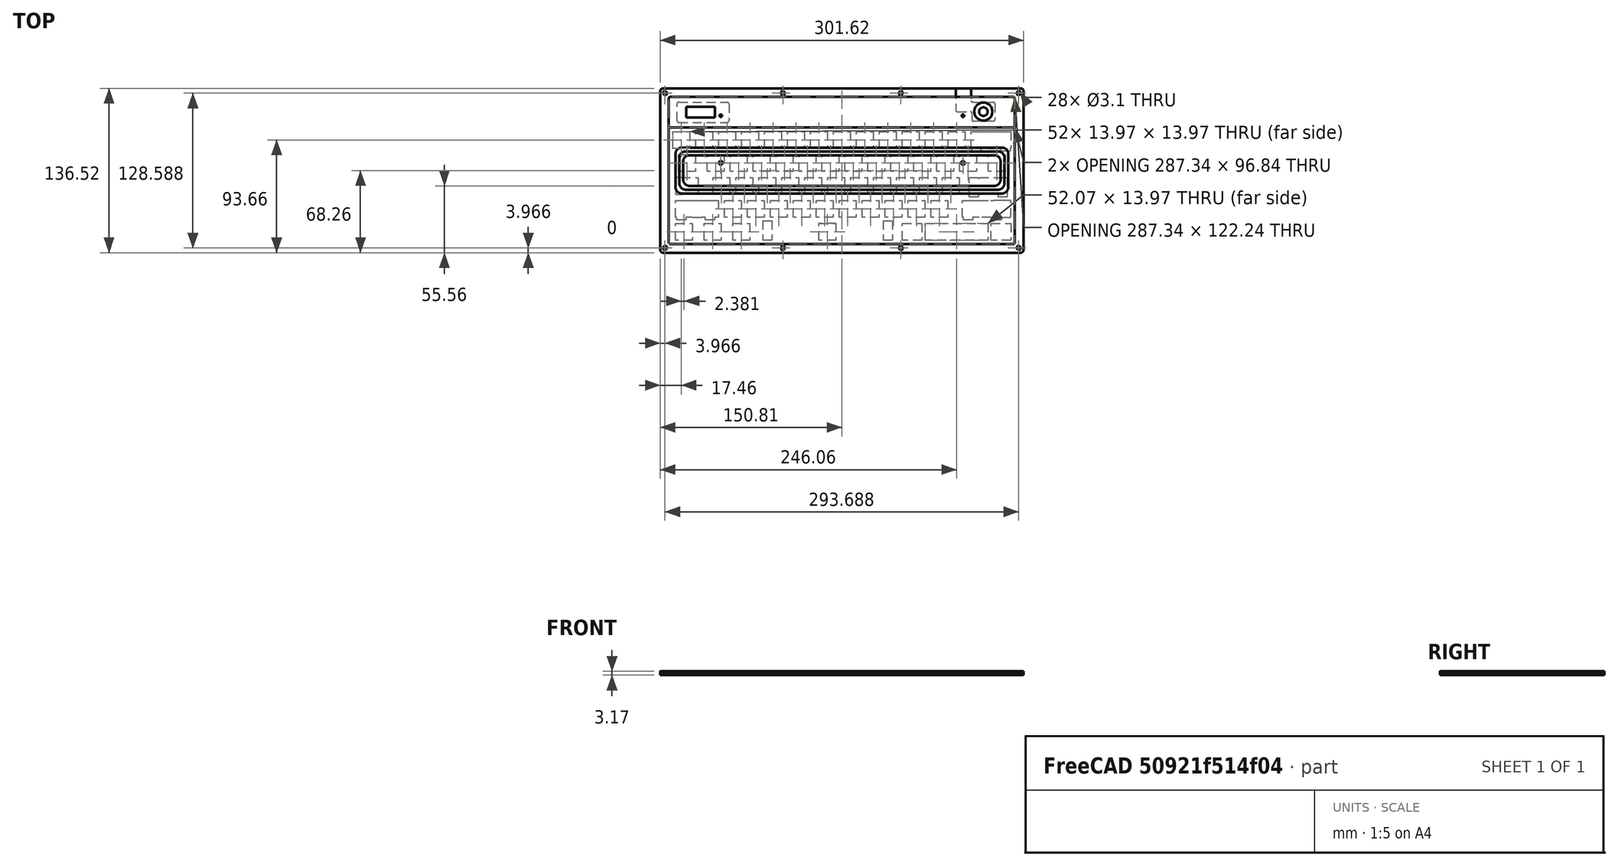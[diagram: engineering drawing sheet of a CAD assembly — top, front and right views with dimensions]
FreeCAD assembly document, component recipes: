
FREECAD ASSEMBLY — COMPONENT RECIPES ("grabert")

This assembly document has 9 components, labeled P0..P8 below (a component is one placed body or linked part). 8 of them carry a construction recipe — the FreeCAD feature program that regenerates the part from scratch, quoted from this document or its linked companion documents; the rest are supplied as boundary geometry only. No exploded tour is included for this assembly.
COMPONENT P0 — recipe-attached ("bottom", modeled in this document).
Construction recipe (the document's own serialized feature program — sketch geometry with constraints, then the solid features built on it; lengths are millimeters unless a unit is written):

FEATURE [PartDesign::CoordinateSystem] LCS_0001
  AttacherType = Attacher::AttachEngine3D
  MapMode = 2
  Support = -> [X_Axis002]
FEATURE [Sketcher::SketchObject] Sketch
  MapMode = 5
  Support = -> [XY_Plane002]
  expr: Constraints[71] = <<Parameters>>.case_screw_hole
  expr: Constraints[60] = <<Parameters>>.case_hole_edge_dist
  expr: Constraints[57] = <<Parameters>>.case_screw_hole
  expr: Constraints[72] = <<Parameters>>.foot_hole_seperation
  expr: Constraints[24] = <<Parameters>>.case_outter_radius
  expr: Constraints[73] = <<Parameters>>.foot_hole_height_from_center
  expr: Constraints[74] = <<Parameters>>.case_height
  expr: Constraints[61] = <<Parameters>>.case_hole_edge_dist
  expr: Constraints[23] = <<Parameters>>.case_width
  sketch-geometry (27):
    g0: ArcOfCircle CenterX=-148.272 CenterY=65.7225 CenterZ=0 NormalX=0 NormalY=0 NormalZ=1 AngleXU=0 Radius=2.54 StartAngle=1.5708 EndAngle=3.1416
    g1: ArcOfCircle CenterX=-148.272 CenterY=-65.7225 CenterZ=0 NormalX=0 NormalY=0 NormalZ=1 AngleXU=0 Radius=2.54 StartAngle=3.14159 EndAngle=4.71239
    g2: ArcOfCircle CenterX=148.272 CenterY=-65.7225 CenterZ=0 NormalX=0 NormalY=0 NormalZ=1 AngleXU=0 Radius=2.54 StartAngle=4.71239 EndAngle=6.28319
    g3: ArcOfCircle CenterX=148.272 CenterY=65.7225 CenterZ=0 NormalX=0 NormalY=0 NormalZ=1 AngleXU=0 Radius=2.54 StartAngle=6.28318 EndAngle=7.85398
    g4: LineSegment StartX=-148.273 StartY=68.2625 StartZ=0 EndX=148.273 EndY=68.2625 EndZ=0
    g5: LineSegment StartX=150.812 StartY=65.7225 StartZ=0 EndX=150.812 EndY=-65.7225 EndZ=0
    g6: LineSegment StartX=-148.273 StartY=-68.2625 StartZ=0 EndX=148.273 EndY=-68.2625 EndZ=0
    g7: LineSegment StartX=-150.812 StartY=-65.7225 StartZ=0 EndX=-150.812 EndY=65.7225 EndZ=0
    g8: Circle CenterX=-100.542 CenterY=45.5083 CenterZ=0 NormalX=0 NormalY=0 NormalZ=1 AngleXU=0 Radius=1.05
    g9: Circle [constr] CenterX=0 CenterY=45.5083 CenterZ=0 NormalX=0 NormalY=0 NormalZ=1 AngleXU=0 Radius=1.05
    g10: Circle CenterX=100.542 CenterY=45.5083 CenterZ=0 NormalX=0 NormalY=0 NormalZ=1 AngleXU=0 Radius=1.05
    g11: Circle CenterX=-146.844 CenterY=-64.2937 CenterZ=0 NormalX=0 NormalY=0 NormalZ=1 AngleXU=0 Radius=1.05
    g12: Circle CenterX=-48.9479 CenterY=-64.2937 CenterZ=0 NormalX=0 NormalY=0 NormalZ=1 AngleXU=0 Radius=1.05
    g13: Circle CenterX=48.9479 CenterY=-64.2937 CenterZ=0 NormalX=0 NormalY=0 NormalZ=1 AngleXU=0 Radius=1.05
    g14: Circle CenterX=146.844 CenterY=-64.2937 CenterZ=0 NormalX=0 NormalY=0 NormalZ=1 AngleXU=0 Radius=1.05
    g15: Circle CenterX=146.844 CenterY=64.2937 CenterZ=0 NormalX=0 NormalY=0 NormalZ=1 AngleXU=0 Radius=1.05
    g16: Circle CenterX=48.9479 CenterY=64.2937 CenterZ=0 NormalX=0 NormalY=0 NormalZ=1 AngleXU=0 Radius=1.05
    g17: Circle CenterX=-48.9479 CenterY=64.2937 CenterZ=0 NormalX=0 NormalY=0 NormalZ=1 AngleXU=0 Radius=1.05
    g18: Circle CenterX=-146.844 CenterY=64.2937 CenterZ=0 NormalX=0 NormalY=0 NormalZ=1 AngleXU=0 Radius=1.05
    g19: LineSegment [constr] StartX=-146.844 StartY=64.2937 StartZ=0 EndX=-48.9479 EndY=64.2937 EndZ=0
    g20: LineSegment [constr] StartX=-48.9479 StartY=64.2937 StartZ=0 EndX=48.9479 EndY=64.2937 EndZ=0
    g21: LineSegment [constr] StartX=48.9479 StartY=64.2937 StartZ=0 EndX=146.844 EndY=64.2937 EndZ=0
    g22: LineSegment [constr] StartX=-146.844 StartY=-64.2937 StartZ=0 EndX=-48.9479 EndY=-64.2937 EndZ=0
    g23: LineSegment [constr] StartX=-48.9479 StartY=-64.2937 StartZ=0 EndX=48.9479 EndY=-64.2937 EndZ=0
    g24: LineSegment [constr] StartX=48.9479 StartY=-64.2937 StartZ=0 EndX=146.844 EndY=-64.2937 EndZ=0
    g25: LineSegment [constr] StartX=-100.542 StartY=45.5083 StartZ=0 EndX=0 EndY=45.5083 EndZ=0
    g26: LineSegment [constr] StartX=0 StartY=45.5083 StartZ=0 EndX=100.542 EndY=45.5083 EndZ=0
  constraints (75):
    c: Coincident(g4,g0)
    c: Coincident(g4,g3)
    c: Coincident(g5,g3)
    c: Coincident(g6,g1)
    c: Coincident(g6,g2)
    c: Coincident(g7,g1)
    c: Coincident(g7,g0)
    c: Coincident(g5,g2)
    c: Vertical(g7)
    c: Vertical(g5)
    c: Horizontal(g4)
    c: Horizontal(g6)
    c: Tangent(g0,g4)
    c: Tangent(g0,g7)
    c: Tangent(g1,g6)
    c: Tangent(g6,g2)
    c: Tangent(g5,g2)
    c: Tangent(g3,g5)
    c: Tangent(g3,g4)
    c: Symmetric(g0,g2,g-1)
    c: Equal(g0,g3)
    c: Equal(g3,g2)
    c: Equal(g2,g1)
    c: DistanceX(g0,g3) = 301.625
    c: Radius(g0) = 2.54
    c: Tangent(g1,g7)
    c: PointOnObject(g9,g-2)
    c: Coincident(g19,g18)
    c: Coincident(g19,g17)
    c: Coincident(g20,g17)
    c: Coincident(g20,g16)
    c: Coincident(g21,g16)
    c: Coincident(g21,g15)
    c: Coincident(g22,g11)
    c: Coincident(g23,g12)
    c: Coincident(g24,g13)
    c: Coincident(g24,g14)
    c: Coincident(g23,g13)
    c: Coincident(g22,g12)
    c: Horizontal(g19)
    c: Horizontal(g20)
    c: Horizontal(g21)
    c: Horizontal(g24)
    c: Horizontal(g23)
    c: Horizontal(g22)
    c: Equal(g19,g20)
    c: Equal(g20,g21)
    c: Equal(g21,g24)
    c: Equal(g24,g23)
    c: Equal(g23,g22)
    c: Equal(g18,g17)
    c: Equal(g17,g16)
    c: Equal(g16,g15)
    c: Equal(g14,g13)
    c: Equal(g13,g12)
    c: Equal(g12,g11)
    c: Equal(g18,g11)
    c: Diameter(g18) = 2.1
    c: Vertical(g12,g17)
    c: Symmetric(g17,g13,g-1)
    c: DistanceY(g2,g14) = 3.96875
    c: DistanceX(g14,g2) = 3.96875
    c: Coincident(g25,g8)
    c: Coincident(g25,g9)
    c: Coincident(g26,g9)
    c: Coincident(g26,g10)
    c: Equal(g25,g26)
    c: Horizontal(g26)
    c: Horizontal(g25)
    c: Equal(g8,g9)
    c: Equal(g9,g10)
    c: Diameter(g8) = 2.1
    c: DistanceX(g26,g26) = 100.542
    c: DistanceY(g-1,g9) = 45.5083
    c: DistanceY(g2,g3) = 136.525
FEATURE [PartDesign::Pad] Pad
  Direction = (1,1,1)
  Length = 3.175
  Length2 = 99.9998
  Profile = -> Sketch
  Type = 0
FEATURE [PartDesign::Body] Body
  Group = -> [LCS_0001,Sketch,Pad]
  Origin = -> Origin002
  Tip = -> Pad
COMPONENT P1 — recipe-attached ("clear_top", modeled in this document).
Construction recipe (the document's own serialized feature program — sketch geometry with constraints, then the solid features built on it; lengths are millimeters unless a unit is written):

FEATURE [PartDesign::CoordinateSystem] LCS_0011
  AttacherType = Attacher::AttachEngine3D
  MapMode = 2
  Support = -> [X_Axis012]
FEATURE [Sketcher::SketchObject] Sketch008
  MapMode = 5
  Support = -> [XY_Plane012]
  expr: Constraints[106] = <<Parameters>>.case_edge_width - <<Parameters>>.case_edge_relief
  expr: Constraints[105] = <<Parameters>>.case_edge_width - <<Parameters>>.case_edge_relief
  expr: Constraints[104] = <<Parameters>>.case_inner_radius
  expr: Constraints[68] = <<Parameters>>.case_edge_width / 2
  expr: Constraints[67] = <<Parameters>>.case_edge_width / 2
  expr: Constraints[108] = <<Parameters>>.pcb_height - 1in + 2 * <<Parameters>>.case_edge_relief
  expr: Constraints[65] = <<Parameters>>.case_screw_hole
  expr: Constraints[34] = <<Parameters>>.case_height
  expr: Constraints[69] = <<Parameters>>.case_edge_width / 2
  expr: Constraints[33] = <<Parameters>>.case_width
  expr: Constraints[23] = <<Parameters>>.case_outter_radius
  sketch-geometry (39):
    g0: ArcOfCircle CenterX=-148.273 CenterY=65.7225 CenterZ=0 NormalX=0 NormalY=0 NormalZ=1 AngleXU=0 Radius=2.54 StartAngle=1.5708 EndAngle=3.14159
    g1: ArcOfCircle CenterX=-148.273 CenterY=-65.7225 CenterZ=0 NormalX=0 NormalY=0 NormalZ=1 AngleXU=0 Radius=2.54 StartAngle=3.14159 EndAngle=4.71239
    g2: ArcOfCircle CenterX=148.273 CenterY=-65.7225 CenterZ=0 NormalX=0 NormalY=0 NormalZ=1 AngleXU=0 Radius=2.54 StartAngle=4.71239 EndAngle=6.28318
    g3: ArcOfCircle CenterX=148.273 CenterY=65.7225 CenterZ=0 NormalX=0 NormalY=0 NormalZ=1 AngleXU=0 Radius=2.54 StartAngle=1.08816e-07 EndAngle=1.57079
    g4: LineSegment StartX=-148.273 StartY=68.2625 StartZ=0 EndX=148.273 EndY=68.2625 EndZ=0
    g5: LineSegment StartX=150.812 StartY=65.7225 StartZ=0 EndX=150.812 EndY=-65.7225 EndZ=0
    g6: LineSegment StartX=148.273 StartY=-68.2625 StartZ=0 EndX=-148.272 EndY=-68.2625 EndZ=0
    g7: LineSegment StartX=-150.812 StartY=-65.7225 StartZ=0 EndX=-150.812 EndY=65.7225 EndZ=0
    g8: GeomPoint X=-150.812 Y=68.2625 Z=0
    g9: GeomPoint X=150.812 Y=68.2625 Z=0
    g10: GeomPoint X=150.812 Y=-68.2625 Z=0
    g11: GeomPoint X=-150.812 Y=-68.2625 Z=0
    g12: Circle CenterX=-146.844 CenterY=64.2937 CenterZ=0 NormalX=0 NormalY=0 NormalZ=1 AngleXU=0 Radius=1.05
    g13: Circle CenterX=-48.9479 CenterY=64.2937 CenterZ=0 NormalX=0 NormalY=0 NormalZ=1 AngleXU=0 Radius=1.05
    g14: Circle CenterX=48.9479 CenterY=64.2937 CenterZ=0 NormalX=0 NormalY=0 NormalZ=1 AngleXU=0 Radius=1.05
    g15: Circle CenterX=146.844 CenterY=64.2937 CenterZ=0 NormalX=0 NormalY=0 NormalZ=1 AngleXU=0 Radius=1.05
    g16: Circle CenterX=-146.844 CenterY=-64.2937 CenterZ=0 NormalX=0 NormalY=0 NormalZ=1 AngleXU=0 Radius=1.05
    g17: Circle CenterX=-48.9479 CenterY=-64.2937 CenterZ=0 NormalX=0 NormalY=0 NormalZ=1 AngleXU=0 Radius=1.05
    g18: Circle CenterX=48.9479 CenterY=-64.2937 CenterZ=0 NormalX=0 NormalY=0 NormalZ=1 AngleXU=0 Radius=1.05
    g19: Circle CenterX=146.844 CenterY=-64.2937 CenterZ=0 NormalX=0 NormalY=0 NormalZ=1 AngleXU=0 Radius=1.05
    g20: LineSegment [constr] StartX=-146.844 StartY=64.2937 StartZ=0 EndX=-48.9479 EndY=64.2937 EndZ=0
    g21: LineSegment [constr] StartX=-48.9479 StartY=64.2937 StartZ=0 EndX=48.9479 EndY=64.2937 EndZ=0
    g22: LineSegment [constr] StartX=48.9479 StartY=64.2937 StartZ=0 EndX=146.844 EndY=64.2937 EndZ=0
    g23: LineSegment [constr] StartX=146.844 StartY=-64.2937 StartZ=0 EndX=48.9479 EndY=-64.2937 EndZ=0
    g24: LineSegment [constr] StartX=48.9479 StartY=-64.2937 StartZ=0 EndX=-48.9479 EndY=-64.2937 EndZ=0
    g25: LineSegment [constr] StartX=-48.9479 StartY=-64.2937 StartZ=0 EndX=-146.844 EndY=-64.2937 EndZ=0
    g26: LineSegment [constr] StartX=-143.669 StartY=61.1187 StartZ=0 EndX=143.669 EndY=61.1187 EndZ=0
    g27: LineSegment [constr] StartX=143.669 StartY=61.1187 StartZ=0 EndX=143.669 EndY=-61.1187 EndZ=0
    g28: LineSegment [constr] StartX=143.669 StartY=-61.1187 StartZ=0 EndX=-143.669 EndY=-61.1187 EndZ=0
    g29: LineSegment [constr] StartX=-143.669 StartY=-61.1187 StartZ=0 EndX=-143.669 EndY=61.1187 EndZ=0
    g30: ArcOfCircle CenterX=-142.399 CenterY=-59.8487 CenterZ=0 NormalX=0 NormalY=0 NormalZ=1 AngleXU=0 Radius=1.27 StartAngle=3.14159 EndAngle=4.71239
    g31: ArcOfCircle CenterX=142.399 CenterY=-59.8487 CenterZ=0 NormalX=0 NormalY=0 NormalZ=1 AngleXU=0 Radius=1.27 StartAngle=4.71239 EndAngle=6.28319
    g32: ArcOfCircle CenterX=142.399 CenterY=34.4488 CenterZ=0 NormalX=0 NormalY=0 NormalZ=1 AngleXU=0 Radius=1.27 StartAngle=6.28319 EndAngle=7.85398
    g33: ArcOfCircle CenterX=-142.399 CenterY=34.4488 CenterZ=0 NormalX=0 NormalY=0 NormalZ=1 AngleXU=0 Radius=1.27 StartAngle=1.5708 EndAngle=3.14159
    g34: LineSegment StartX=-143.669 StartY=34.4488 StartZ=0 EndX=-143.669 EndY=-59.8487 EndZ=0
    g35: LineSegment StartX=-142.399 StartY=-61.1187 StartZ=0 EndX=142.399 EndY=-61.1187 EndZ=0
    g36: LineSegment StartX=143.669 StartY=34.4487 StartZ=0 EndX=143.669 EndY=-59.8488 EndZ=0
    g37: LineSegment StartX=142.399 StartY=35.7188 StartZ=0 EndX=-142.399 EndY=35.7188 EndZ=0
    g38: Circle CenterX=117.475 CenterY=48.895 CenterZ=0 NormalX=0 NormalY=0 NormalZ=1 AngleXU=0 Radius=7.50062
  constraints (112):
    c: Vertical(g7)
    c: Vertical(g5)
    c: Horizontal(g4)
    c: Horizontal(g6)
    c: Coincident(g0,g4)
    c: Coincident(g0,g7)
    c: Coincident(g7,g1)
    c: Coincident(g1,g6)
    c: Coincident(g6,g2)
    c: Coincident(g5,g2)
    c: Coincident(g5,g3)
    c: Coincident(g3,g4)
    c: Tangent(g0,g4)
    c: Tangent(g0,g7)
    c: Tangent(g7,g1)
    c: Tangent(g1,g6)
    c: Tangent(g6,g2)
    c: Tangent(g2,g5)
    c: Tangent(g5,g3)
    c: Tangent(g3,g4)
    c: Equal(g0,g3)
    c: Equal(g3,g2)
    c: Equal(g2,g1)
    c: Radius(g0) = 2.54
    c: PointOnObject(g8,g4)
    c: PointOnObject(g8,g7)
    c: PointOnObject(g11,g7)
    c: PointOnObject(g11,g6)
    c: PointOnObject(g10,g6)
    c: PointOnObject(g10,g5)
    c: PointOnObject(g9,g5)
    c: PointOnObject(g9,g4)
    c: Symmetric(g8,g10,g-1)
    c: DistanceX(g8,g10) = 301.625
    c: DistanceY(g10,g8) = 136.525
    c: Horizontal(g20)
    c: Horizontal(g21)
    c: Horizontal(g22)
    c: Horizontal(g23)
    c: Horizontal(g24)
    c: Horizontal(g25)
    c: Coincident(g20,g12)
    c: Coincident(g20,g13)
    c: Coincident(g21,g13)
    c: Coincident(g21,g14)
    c: Coincident(g22,g14)
    c: Coincident(g22,g15)
    c: Coincident(g25,g16)
    c: Coincident(g25,g17)
    c: Coincident(g24,g17)
    c: Coincident(g24,g18)
    c: Coincident(g18,g23)
    c: Coincident(g19,g23)
    c: Equal(g20,g21)
    c: Equal(g21,g22)
    c: Equal(g22,g23)
    c: Equal(g23,g24)
    c: Equal(g24,g25)
    c: Equal(g12,g13)
    c: Equal(g13,g14)
    c: Equal(g14,g15)
    c: Equal(g15,g19)
    c: Equal(g19,g18)
    c: Equal(g18,g17)
    c: Equal(g17,g16)
    c: Diameter(g12) = 2.1
    c: Symmetric(g12,g19,g-1)
    c: DistanceX(g8,g12) = 3.96875
    c: DistanceY(g12,g8) = 3.96875
    c: DistanceX(g11,g16) = 3.96875
    c: Coincident(g26,g27)
    c: Coincident(g27,g28)
    c: Coincident(g28,g29)
    c: Coincident(g29,g26)
    c: Horizontal(g26)
    c: Horizontal(g28)
    c: Vertical(g27)
    c: Vertical(g29)
    c: Coincident(g37,g33)
    c: Coincident(g33,g34)
    c: Coincident(g34,g30)
    c: Coincident(g30,g35)
    c: Coincident(g35,g31)
    c: Coincident(g31,g36)
    c: Coincident(g36,g32)
    c: Coincident(g32,g37)
    c: Tangent(g37,g33)
    c: Tangent(g33,g34)
    c: Tangent(g34,g30)
    c: Tangent(g30,g35)
    c: Tangent(g35,g31)
    c: Tangent(g31,g36)
    c: Tangent(g36,g32)
    c: Tangent(g32,g37)
    c: PointOnObject(g33,g29)
    c: PointOnObject(g30,g29)
    c: PointOnObject(g30,g28)
    c: PointOnObject(g31,g28)
    c: PointOnObject(g31,g27)
    c: PointOnObject(g32,g27)
    c: Horizontal(g37)
    c: Equal(g30,g33)
    c: Equal(g33,g32)
    c: Equal(g32,g31)
    c: Radius(g33) = 1.27
    c: DistanceX(g11,g28) = 7.14375
    c: DistanceY(g11,g28) = 7.14375
    c: Symmetric(g26,g27,g-1)
    c: DistanceY(g30,g33) = 96.8375
    c: Diameter(g38) = 15.0012
    c: DistanceY(g38,g9) = 19.3675
    c: DistanceX(g38,g9) = 33.3375
FEATURE [PartDesign::Pad] Pad005
  Direction = (1,1,1)
  Length = 3.175
  Length2 = 99.9998
  Profile = -> Sketch008
  Type = 0
FEATURE [PartDesign::Body] Body_6
  Group = -> [LCS_0011,Sketch008,Pad005]
  Origin = -> Origin012
  Tip = -> Pad005
COMPONENT P2 — recipe-attached ("closed_spacer", modeled in this document).
Construction recipe (the document's own serialized feature program — sketch geometry with constraints, then the solid features built on it; lengths are millimeters unless a unit is written):

FEATURE [PartDesign::CoordinateSystem] LCS_0003
  AttacherType = Attacher::AttachEngine3D
  MapMode = 2
  Support = -> [X_Axis004]
FEATURE [Sketcher::SketchObject] Sketch001
  MapMode = 5
  Support = -> [XY_Plane004]
  expr: Constraints[23] = <<Parameters>>.case_outter_radius
  expr: Constraints[24] = <<Parameters>>.case_width
  expr: Constraints[25] = <<Parameters>>.case_height
  expr: Constraints[51] = <<Parameters>>.case_edge_width - <<Parameters>>.case_edge_relief
  expr: Constraints[50] = <<Parameters>>.case_inner_radius
  expr: Constraints[52] = <<Parameters>>.case_edge_width - <<Parameters>>.case_edge_relief
  expr: Constraints[53] = <<Parameters>>.case_edge_width - <<Parameters>>.case_edge_relief
  expr: Constraints[54] = <<Parameters>>.case_edge_width - <<Parameters>>.case_edge_relief
  expr: Constraints[86] = <<Parameters>>.case_spacer_hole
  expr: Constraints[88] = <<Parameters>>.case_hole_edge_dist
  expr: Constraints[87] = <<Parameters>>.case_hole_edge_dist
  expr: Constraints[89] = <<Parameters>>.case_hole_edge_dist
  sketch-geometry (30):
    g0: ArcOfCircle CenterX=-148.273 CenterY=65.7225 CenterZ=0 NormalX=0 NormalY=0 NormalZ=1 AngleXU=0 Radius=2.54 StartAngle=1.5708 EndAngle=3.1416
    g1: ArcOfCircle CenterX=-148.273 CenterY=-65.7225 CenterZ=0 NormalX=0 NormalY=0 NormalZ=1 AngleXU=0 Radius=2.54 StartAngle=3.14159 EndAngle=4.71239
    g2: ArcOfCircle CenterX=148.272 CenterY=-65.7225 CenterZ=0 NormalX=0 NormalY=0 NormalZ=1 AngleXU=0 Radius=2.54 StartAngle=4.71239 EndAngle=6.28319
    g3: ArcOfCircle CenterX=148.272 CenterY=65.7225 CenterZ=0 NormalX=0 NormalY=0 NormalZ=1 AngleXU=0 Radius=2.54 StartAngle=6.28318 EndAngle=7.85398
    g4: LineSegment StartX=-150.813 StartY=65.7225 StartZ=0 EndX=-150.813 EndY=-65.7225 EndZ=0
    g5: LineSegment StartX=-148.273 StartY=68.2625 StartZ=0 EndX=148.273 EndY=68.2625 EndZ=0
    g6: LineSegment StartX=150.812 StartY=65.7225 StartZ=0 EndX=150.812 EndY=-65.7225 EndZ=0
    g7: LineSegment StartX=-148.273 StartY=-68.2625 StartZ=0 EndX=148.273 EndY=-68.2625 EndZ=0
    g8: ArcOfCircle CenterX=-142.399 CenterY=59.8487 CenterZ=0 NormalX=0 NormalY=0 NormalZ=1 AngleXU=0 Radius=1.27 StartAngle=1.5708 EndAngle=3.14159
    g9: ArcOfCircle CenterX=-142.399 CenterY=-59.8487 CenterZ=0 NormalX=0 NormalY=0 NormalZ=1 AngleXU=0 Radius=1.27 StartAngle=3.14159 EndAngle=4.71239
    g10: ArcOfCircle CenterX=142.399 CenterY=-59.8487 CenterZ=0 NormalX=0 NormalY=0 NormalZ=1 AngleXU=0 Radius=1.27 StartAngle=4.71239 EndAngle=6.28319
    g11: ArcOfCircle CenterX=142.399 CenterY=59.8487 CenterZ=0 NormalX=0 NormalY=0 NormalZ=1 AngleXU=0 Radius=1.27 StartAngle=6.28319 EndAngle=7.85398
    g12: LineSegment StartX=143.669 StartY=59.8487 StartZ=0 EndX=143.669 EndY=-59.8488 EndZ=0
    g13: LineSegment StartX=142.399 StartY=-61.1187 StartZ=0 EndX=-142.399 EndY=-61.1187 EndZ=0
    g14: LineSegment StartX=142.399 StartY=61.1187 StartZ=0 EndX=-142.399 EndY=61.1187 EndZ=0
    g15: LineSegment StartX=-143.669 StartY=59.8488 StartZ=0 EndX=-143.669 EndY=-59.8487 EndZ=0
    g16: Circle CenterX=-146.844 CenterY=64.2937 CenterZ=0 NormalX=0 NormalY=0 NormalZ=1 AngleXU=0 Radius=1.55
    g17: Circle CenterX=-48.9479 CenterY=64.2937 CenterZ=0 NormalX=0 NormalY=0 NormalZ=1 AngleXU=0 Radius=1.55
    g18: Circle CenterX=48.9479 CenterY=64.2937 CenterZ=0 NormalX=0 NormalY=0 NormalZ=1 AngleXU=0 Radius=1.55
    g19: Circle CenterX=146.844 CenterY=64.2937 CenterZ=0 NormalX=0 NormalY=0 NormalZ=1 AngleXU=0 Radius=1.55
    g20: Circle CenterX=146.844 CenterY=-64.2937 CenterZ=0 NormalX=0 NormalY=0 NormalZ=1 AngleXU=0 Radius=1.55
    g21: Circle CenterX=48.9479 CenterY=-64.2937 CenterZ=0 NormalX=0 NormalY=0 NormalZ=1 AngleXU=0 Radius=1.55
    g22: Circle CenterX=-48.9479 CenterY=-64.2937 CenterZ=0 NormalX=0 NormalY=0 NormalZ=1 AngleXU=0 Radius=1.55
    g23: Circle CenterX=-146.844 CenterY=-64.2937 CenterZ=0 NormalX=0 NormalY=0 NormalZ=1 AngleXU=0 Radius=1.55
    g24: LineSegment [constr] StartX=-146.844 StartY=64.2937 StartZ=0 EndX=-48.9479 EndY=64.2937 EndZ=0
    g25: LineSegment [constr] StartX=-48.9479 StartY=64.2937 StartZ=0 EndX=48.9479 EndY=64.2937 EndZ=0
    g26: LineSegment [constr] StartX=48.9479 StartY=64.2937 StartZ=0 EndX=146.844 EndY=64.2937 EndZ=0
    g27: LineSegment [constr] StartX=146.844 StartY=-64.2937 StartZ=0 EndX=48.9479 EndY=-64.2937 EndZ=0
    g28: LineSegment [constr] StartX=48.9479 StartY=-64.2937 StartZ=0 EndX=-48.9479 EndY=-64.2937 EndZ=0
    g29: LineSegment [constr] StartX=-48.9479 StartY=-64.2937 StartZ=0 EndX=-146.844 EndY=-64.2937 EndZ=0
  constraints (90):
    c: Coincident(g0,g5)
    c: Coincident(g4,g0)
    c: Coincident(g4,g1)
    c: Coincident(g7,g1)
    c: Coincident(g7,g2)
    c: Coincident(g6,g2)
    c: Coincident(g6,g3)
    c: Coincident(g5,g3)
    c: Tangent(g5,g3)
    c: Tangent(g3,g6)
    c: Tangent(g6,g2)
    c: Tangent(g2,g7)
    c: Tangent(g7,g1)
    c: Tangent(g1,g4)
    c: Tangent(g0,g4)
    c: Tangent(g5,g0)
    c: Horizontal(g5)
    c: Horizontal(g7)
    c: Vertical(g4)
    c: Vertical(g6)
    c: Equal(g0,g3)
    c: Equal(g3,g2)
    c: Equal(g2,g1)
    c: Radius(g0) = 2.54
    c: DistanceX(g0,g3) = 301.625
    c: DistanceY(g2,g3) = 136.525
    c: Symmetric(g0,g2,g-1)
    c: Coincident(g15,g8)
    c: Coincident(g15,g9)
    c: Coincident(g9,g13)
    c: Coincident(g14,g8)
    c: Coincident(g11,g14)
    c: Coincident(g11,g12)
    c: Coincident(g12,g10)
    c: Coincident(g10,g13)
    c: Tangent(g8,g14)
    c: Tangent(g14,g11)
    c: Tangent(g11,g12)
    c: Tangent(g12,g10)
    c: Tangent(g10,g13)
    c: Tangent(g13,g9)
    c: Tangent(g9,g15)
    c: Tangent(g15,g8)
    c: Vertical(g15)
    c: Vertical(g12)
    c: Horizontal(g14)
    c: Horizontal(g13)
    c: Equal(g8,g11)
    c: Equal(g11,g10)
    c: Equal(g9,g10)
    c: Radius(g8) = 1.27
    c: DistanceY(g8,g0) = 7.14375
    c: DistanceX(g0,g8) = 7.14375
    c: DistanceX(g10,g2) = 7.14375
    c: DistanceY(g2,g10) = 7.14375
    c: Equal(g16,g17)
    c: Equal(g17,g18)
    c: Equal(g18,g19)
    c: Equal(g19,g20)
    c: Equal(g20,g21)
    c: Equal(g21,g22)
    c: Equal(g22,g23)
    c: Equal(g24,g25)
    c: Equal(g25,g26)
    c: Equal(g26,g27)
    c: Equal(g27,g28)
    c: Equal(g28,g29)
    c: Coincident(g24,g16)
    c: Coincident(g24,g17)
    c: Coincident(g25,g17)
    c: Coincident(g25,g18)
    c: Coincident(g18,g26)
    c: Coincident(g26,g19)
    c: Coincident(g27,g20)
    c: Coincident(g27,g21)
    c: Coincident(g28,g21)
    c: Coincident(g28,g22)
    c: Coincident(g29,g22)
    c: Coincident(g23,g29)
    c: Horizontal(g24)
    c: Horizontal(g25)
    c: Horizontal(g26)
    c: Horizontal(g27)
    c: Horizontal(g28)
    c: Horizontal(g29)
    c: Symmetric(g17,g21,g-1)
    c: Diameter(g16) = 3.1
    c: DistanceX(g20,g2) = 3.96875
    c: DistanceY(g2,g20) = 3.96875
    c: DistanceX(g1,g23) = 3.96875
FEATURE [PartDesign::Pad] Pad001
  Direction = (1,1,1)
  Length = 3.175
  Length2 = 99.9998
  Profile = -> Sketch001
  Type = 0
FEATURE [PartDesign::Body] Body_2
  Group = -> [LCS_0003,Sketch001,Pad001]
  Origin = -> Origin004
  Tip = -> Pad001
COMPONENT P3 — recipe-attached ("colored_top", modeled in this document).
Construction recipe (the document's own serialized feature program — sketch geometry with constraints, then the solid features built on it; lengths are millimeters unless a unit is written):

FEATURE [PartDesign::CoordinateSystem] LCS_0009
  AttacherType = Attacher::AttachEngine3D
  MapMode = 2
  Support = -> [X_Axis010]
FEATURE [Sketcher::SketchObject] Sketch007
  MapMode = 5
  Support = -> [XY_Plane010]
  expr: Constraints[118] = <<Parameters>>.case_edge_width / 2
  expr: Constraints[119] = <<Parameters>>.case_edge_width / 2
  expr: Constraints[117] = <<Parameters>>.case_edge_width / 2
  expr: Constraints[73] = <<Parameters>>.case_edge_width - <<Parameters>>.case_edge_relief
  expr: Constraints[110] = <<Parameters>>.case_spacer_hole
  expr: Constraints[72] = <<Parameters>>.case_edge_width - <<Parameters>>.case_edge_relief
  expr: Constraints[67] = <<Parameters>>.case_height
  expr: Constraints[68] = <<Parameters>>.case_outter_radius
  expr: Constraints[69] = <<Parameters>>.case_width
  expr: Constraints[71] = <<Parameters>>.pcb_height - 1in + 2 * <<Parameters>>.case_edge_relief
  expr: Constraints[70] = <<Parameters>>.case_inner_radius
  sketch-geometry (41):
    g0: ArcOfCircle CenterX=-148.272 CenterY=65.7225 CenterZ=0 NormalX=0 NormalY=0 NormalZ=1 AngleXU=0 Radius=2.54 StartAngle=1.5708 EndAngle=3.1416
    g1: ArcOfCircle CenterX=-148.272 CenterY=-65.7225 CenterZ=0 NormalX=0 NormalY=0 NormalZ=1 AngleXU=0 Radius=2.54 StartAngle=3.14159 EndAngle=4.71239
    g2: ArcOfCircle CenterX=148.272 CenterY=-65.7225 CenterZ=0 NormalX=0 NormalY=0 NormalZ=1 AngleXU=0 Radius=2.54 StartAngle=4.71239 EndAngle=6.28319
    g3: ArcOfCircle CenterX=148.273 CenterY=65.7225 CenterZ=0 NormalX=0 NormalY=0 NormalZ=1 AngleXU=0 Radius=2.54 StartAngle=6.28318 EndAngle=7.85398
    g4: LineSegment StartX=-148.273 StartY=68.2625 StartZ=0 EndX=148.273 EndY=68.2625 EndZ=0
    g5: LineSegment StartX=150.812 StartY=65.7225 StartZ=0 EndX=150.812 EndY=-65.7225 EndZ=0
    g6: LineSegment StartX=148.272 StartY=-68.2625 StartZ=0 EndX=-148.273 EndY=-68.2625 EndZ=0
    g7: LineSegment StartX=-150.812 StartY=-65.7225 StartZ=0 EndX=-150.812 EndY=65.7225 EndZ=0
    g8: ArcOfCircle CenterX=-142.399 CenterY=34.4487 CenterZ=0 NormalX=0 NormalY=0 NormalZ=1 AngleXU=0 Radius=1.27 StartAngle=1.5708 EndAngle=3.14159
    g9: ArcOfCircle CenterX=-142.399 CenterY=-59.8488 CenterZ=0 NormalX=0 NormalY=0 NormalZ=1 AngleXU=0 Radius=1.27 StartAngle=3.14159 EndAngle=4.71239
    g10: ArcOfCircle CenterX=142.399 CenterY=-59.8488 CenterZ=0 NormalX=0 NormalY=0 NormalZ=1 AngleXU=0 Radius=1.27 StartAngle=4.71239 EndAngle=6.28319
    g11: ArcOfCircle CenterX=142.399 CenterY=34.4487 CenterZ=0 NormalX=0 NormalY=0 NormalZ=1 AngleXU=0 Radius=1.27 StartAngle=1.02571e-07 EndAngle=1.5708
    g12: LineSegment StartX=-129.089 StartY=52.9895 StartZ=0 EndX=-105.366 EndY=52.9895 EndZ=0
    g13: LineSegment StartX=-105.366 StartY=52.9895 StartZ=0 EndX=-105.366 EndY=43.9776 EndZ=0
    g14: LineSegment StartX=-105.366 StartY=43.9776 StartZ=0 EndX=-129.089 EndY=43.9776 EndZ=0
    g15: LineSegment StartX=-129.089 StartY=43.9776 StartZ=0 EndX=-129.089 EndY=52.9895 EndZ=0
    g16: Circle CenterX=117.475 CenterY=48.895 CenterZ=0 NormalX=0 NormalY=0 NormalZ=1 AngleXU=0 Radius=3.60045
    g17: LineSegment StartX=-142.399 StartY=35.7187 StartZ=0 EndX=142.399 EndY=35.7187 EndZ=0
    g18: LineSegment StartX=-143.669 StartY=34.4487 StartZ=0 EndX=-143.669 EndY=-59.8488 EndZ=0
    g19: LineSegment StartX=-142.399 StartY=-61.1188 StartZ=0 EndX=142.399 EndY=-61.1188 EndZ=0
    g20: LineSegment StartX=143.669 StartY=-59.8488 StartZ=0 EndX=143.669 EndY=34.4488 EndZ=0
    g21: LineSegment [constr] StartX=-143.669 StartY=61.1187 StartZ=0 EndX=143.669 EndY=61.1187 EndZ=0
    g22: LineSegment [constr] StartX=143.669 StartY=61.1187 StartZ=0 EndX=143.669 EndY=-61.1187 EndZ=0
    g23: LineSegment [constr] StartX=143.669 StartY=-61.1187 StartZ=0 EndX=-143.669 EndY=-61.1187 EndZ=0
    g24: LineSegment [constr] StartX=-143.669 StartY=-61.1187 StartZ=0 EndX=-143.669 EndY=61.1187 EndZ=0
    g25: GeomPoint X=-150.812 Y=68.2625 Z=0
    g26: GeomPoint X=150.812 Y=68.2625 Z=0
    g27: Circle CenterX=-146.844 CenterY=64.2937 CenterZ=0 NormalX=0 NormalY=0 NormalZ=1 AngleXU=0 Radius=1.55
    g28: Circle CenterX=-48.9479 CenterY=64.2937 CenterZ=0 NormalX=0 NormalY=0 NormalZ=1 AngleXU=0 Radius=1.55
    g29: Circle CenterX=48.9479 CenterY=64.2937 CenterZ=0 NormalX=0 NormalY=0 NormalZ=1 AngleXU=0 Radius=1.55
    g30: Circle CenterX=146.844 CenterY=64.2937 CenterZ=0 NormalX=0 NormalY=0 NormalZ=1 AngleXU=0 Radius=1.55
    g31: Circle CenterX=-146.844 CenterY=-64.2937 CenterZ=0 NormalX=0 NormalY=0 NormalZ=1 AngleXU=0 Radius=1.55
    g32: Circle CenterX=-48.9479 CenterY=-64.2937 CenterZ=0 NormalX=0 NormalY=0 NormalZ=1 AngleXU=0 Radius=1.55
    g33: Circle CenterX=48.9479 CenterY=-64.2937 CenterZ=0 NormalX=0 NormalY=0 NormalZ=1 AngleXU=0 Radius=1.55
    g34: Circle CenterX=146.844 CenterY=-64.2937 CenterZ=0 NormalX=0 NormalY=0 NormalZ=1 AngleXU=0 Radius=1.55
    g35: LineSegment [constr] StartX=-146.844 StartY=64.2937 StartZ=0 EndX=-48.9479 EndY=64.2937 EndZ=0
    g36: LineSegment [constr] StartX=-48.9479 StartY=64.2937 StartZ=0 EndX=48.9479 EndY=64.2937 EndZ=0
    g37: LineSegment [constr] StartX=48.9479 StartY=64.2937 StartZ=0 EndX=146.844 EndY=64.2937 EndZ=0
    g38: LineSegment [constr] StartX=-146.844 StartY=-64.2937 StartZ=0 EndX=-48.9479 EndY=-64.2937 EndZ=0
    g39: LineSegment [constr] StartX=-48.9479 StartY=-64.2937 StartZ=0 EndX=48.9479 EndY=-64.2937 EndZ=0
    g40: LineSegment [constr] StartX=48.9479 StartY=-64.2937 StartZ=0 EndX=146.844 EndY=-64.2937 EndZ=0
  constraints (120):
    c: Coincident(g12,g13)
    c: Coincident(g13,g14)
    c: Coincident(g14,g15)
    c: Coincident(g15,g12)
    c: Horizontal(g12)
    c: Horizontal(g14)
    c: Vertical(g13)
    c: Vertical(g15)
    c: Coincident(g0,g4)
    c: Coincident(g0,g7)
    c: Coincident(g7,g1)
    c: Coincident(g1,g6)
    c: Coincident(g6,g2)
    c: Coincident(g2,g5)
    c: Coincident(g5,g3)
    c: Coincident(g3,g4)
    c: Coincident(g8,g17)
    c: Coincident(g8,g18)
    c: Coincident(g18,g9)
    c: Coincident(g9,g19)
    c: Coincident(g19,g10)
    c: Coincident(g10,g20)
    c: Coincident(g11,g20)
    c: Coincident(g11,g17)
    c: Horizontal(g17)
    c: Horizontal(g19)
    c: Horizontal(g6)
    c: Horizontal(g4)
    c: Vertical(g7)
    c: Vertical(g5)
    c: Vertical(g20)
    c: Vertical(g18)
    c: Tangent(g4,g0)
    c: Tangent(g0,g7)
    c: Tangent(g7,g1)
    c: Tangent(g1,g6)
    c: Tangent(g6,g2)
    c: Tangent(g2,g5)
    c: Tangent(g5,g3)
    c: Tangent(g3,g4)
    c: Tangent(g17,g11)
    c: Tangent(g11,g20)
    c: Tangent(g20,g10)
    c: Tangent(g10,g19)
    c: Tangent(g19,g9)
    c: Tangent(g9,g18)
    c: Tangent(g18,g8)
    c: Tangent(g8,g17)
    c: Equal(g0,g3)
    c: Equal(g3,g2)
    c: Equal(g2,g1)
    c: Equal(g8,g9)
    c: Equal(g9,g10)
    c: Equal(g10,g11)
    c: Symmetric(g0,g2,g-1)
    c: Coincident(g21,g22)
    c: Coincident(g22,g23)
    c: Coincident(g23,g24)
    c: Coincident(g24,g21)
    c: Horizontal(g21)
    c: Horizontal(g23)
    c: Vertical(g22)
    c: Vertical(g24)
    c: PointOnObject(g9,g24)
    c: PointOnObject(g9,g23)
    c: PointOnObject(g11,g22)
    c: Symmetric(g21,g22,g-1)
    c: DistanceY(g1,g0) = 136.525
    c: Radius(g0) = 2.54
    c: DistanceX(g0,g3) = 301.625
    c: Radius(g8) = 1.27
    c: DistanceY(g9,g8) = 96.8375
    c: DistanceY(g1,g9) = 7.14375
    c: DistanceX(g1,g23) = 7.14375
    c: PointOnObject(g25,g4)
    c: PointOnObject(g25,g7)
    c: DistanceX(g25,g12) = 21.7233
    c: DistanceY(g12,g25) = 15.273
    c: DistanceY(g13,g13) = 9.01192
    c: DistanceX(g14,g14) = 23.7236
    c: PointOnObject(g26,g4)
    c: PointOnObject(g26,g5)
    c: DistanceX(g16,g26) = 33.3375
    c: DistanceY(g16,g26) = 19.3675
    c: Diameter(g16) = 7.2009
    c: Coincident(g35,g27)
    c: Coincident(g35,g28)
    c: Coincident(g36,g28)
    c: Coincident(g36,g29)
    c: Coincident(g37,g29)
    c: Coincident(g37,g30)
    c: Horizontal(g37)
    c: Horizontal(g36)
    c: Horizontal(g35)
    c: Horizontal(g38)
    c: Horizontal(g39)
    c: Horizontal(g40)
    c: Coincident(g38,g31)
    c: Coincident(g32,g38)
    c: Coincident(g39,g32)
    c: Coincident(g33,g39)
    c: Coincident(g40,g33)
    c: Coincident(g34,g40)
    c: Equal(g31,g32)
    c: Equal(g32,g33)
    c: Equal(g33,g34)
    c: Equal(g34,g30)
    c: Equal(g30,g29)
    c: Equal(g29,g28)
    c: Equal(g28,g27)
    c: Diameter(g27) = 3.1
    c: Equal(g35,g36)
    c: Equal(g36,g37)
    c: Equal(g37,g38)
    c: Equal(g38,g39)
    c: Equal(g39,g40)
    c: Symmetric(g28,g33,g-1)
    c: DistanceY(g27,g25) = 3.96875
    c: DistanceX(g25,g27) = 3.96875
    c: DistanceX(g25,g31) = 3.96875
FEATURE [PartDesign::Pad] Pad004
  Direction = (1,1,1)
  Length = 3.175
  Length2 = 99.9998
  Profile = -> Sketch007
  Type = 0
FEATURE [PartDesign::Body] Body_5
  Group = -> [LCS_0009,Sketch007,Pad004]
  Origin = -> Origin010
  Tip = -> Pad004
COMPONENT P4 — recipe-attached ("foot_0", modeled in this document).
Construction recipe (the document's own serialized feature program — sketch geometry with constraints, then the solid features built on it; lengths are millimeters unless a unit is written):

FEATURE [PartDesign::CoordinateSystem] LCS_0013
  AttacherType = Attacher::AttachEngine3D
  MapMode = 2
  Support = -> [X_Axis014]
FEATURE [Sketcher::SketchObject] Sketch009
  MapMode = 5
  Support = -> [XY_Plane014]
  expr: Constraints[23] = <<Parameters>>.case_outter_radius * 2
  expr: Constraints[30] = <<Parameters>>.case_width - 1in
  expr: Constraints[38] = <<Parameters>>.case_spacer_hole
  expr: Constraints[39] = <<Parameters>>.foot_hole_seperation * 2
  sketch-geometry (14):
    g0: ArcOfCircle CenterX=-133.032 CenterY=13.97 CenterZ=0 NormalX=0 NormalY=0 NormalZ=1 AngleXU=0 Radius=5.08 StartAngle=1.57079 EndAngle=3.14159
    g1: ArcOfCircle CenterX=-133.032 CenterY=-13.97 CenterZ=0 NormalX=0 NormalY=0 NormalZ=1 AngleXU=0 Radius=5.08 StartAngle=3.14159 EndAngle=4.71239
    g2: ArcOfCircle CenterX=133.033 CenterY=-13.97 CenterZ=0 NormalX=0 NormalY=0 NormalZ=1 AngleXU=0 Radius=5.08 StartAngle=4.71238 EndAngle=6.28319
    g3: ArcOfCircle CenterX=133.033 CenterY=13.97 CenterZ=0 NormalX=0 NormalY=0 NormalZ=1 AngleXU=0 Radius=5.08 StartAngle=2.61338e-07 EndAngle=1.5708
    g4: LineSegment StartX=-133.032 StartY=19.05 StartZ=0 EndX=133.032 EndY=19.05 EndZ=0
    g5: LineSegment StartX=138.112 StartY=13.97 StartZ=0 EndX=138.112 EndY=-13.97 EndZ=0
    g6: LineSegment StartX=133.032 StartY=-19.05 StartZ=0 EndX=-133.032 EndY=-19.05 EndZ=0
    g7: LineSegment StartX=-138.112 StartY=-13.97 StartZ=0 EndX=-138.112 EndY=13.97 EndZ=0
    g8: GeomPoint X=-138.113 Y=19.05 Z=0
    g9: GeomPoint X=138.113 Y=-19.05 Z=0
    g10: Circle CenterX=-100.542 CenterY=6.35 CenterZ=0 NormalX=0 NormalY=0 NormalZ=1 AngleXU=0 Radius=1.55
    g11: Circle CenterX=100.542 CenterY=6.35 CenterZ=0 NormalX=0 NormalY=0 NormalZ=1 AngleXU=0 Radius=1.55
    g12: LineSegment [constr] StartX=-100.542 StartY=6.35 StartZ=0 EndX=100.542 EndY=6.35 EndZ=0
    g13: GeomPoint X=0 Y=6.35 Z=0
  constraints (40):
    c: Coincident(g0,g4)
    c: Coincident(g0,g7)
    c: Coincident(g7,g1)
    c: Coincident(g1,g6)
    c: Coincident(g6,g2)
    c: Coincident(g2,g5)
    c: Coincident(g5,g3)
    c: Coincident(g4,g3)
    c: Horizontal(g4)
    c: Horizontal(g6)
    c: Vertical(g7)
    c: Vertical(g5)
    c: Tangent(g0,g4)
    c: Tangent(g0,g7)
    c: Tangent(g7,g1)
    c: Tangent(g6,g1)
    c: Tangent(g6,g2)
    c: Tangent(g2,g5)
    c: Tangent(g5,g3)
    c: Tangent(g3,g4)
    c: Equal(g0,g3)
    c: Equal(g3,g2)
    c: Equal(g2,g1)
    c: Radius(g3) = 5.08
    c: PointOnObject(g8,g4)
    c: PointOnObject(g8,g7)
    c: PointOnObject(g9,g6)
    c: PointOnObject(g9,g5)
    c: Symmetric(g8,g9,g-1)
    c: DistanceY(g9,g8) = 38.1
    c: DistanceX(g8,g9) = 276.225
    c: Coincident(g12,g10)
    c: Coincident(g12,g11)
    c: Horizontal(g12)
    c: Symmetric(g10,g11,g13)
    c: PointOnObject(g13,g-2)
    c: DistanceY(g-1,g13) = 6.35
    c: Equal(g10,g11)
    c: Diameter(g10) = 3.1
    c: DistanceX(g12,g12) = 201.083
FEATURE [PartDesign::Pad] Pad006
  Direction = (1,1,1)
  Length = 3.175
  Length2 = 99.9998
  Profile = -> Sketch009
  Type = 0
FEATURE [PartDesign::Body] Body_7
  Group = -> [LCS_0013,Sketch009,Pad006]
  Origin = -> Origin014
  Tip = -> Pad006
COMPONENT P5 — recipe-attached ("foot_1", modeled in this document).
Construction recipe (the document's own serialized feature program — sketch geometry with constraints, then the solid features built on it; lengths are millimeters unless a unit is written):

FEATURE [PartDesign::CoordinateSystem] LCS_0016
  AttacherType = Attacher::AttachEngine3D
  MapMode = 2
  Support = -> [X_Axis017]
FEATURE [Sketcher::SketchObject] Sketch010
  MapMode = 5
  Support = -> [XY_Plane017]
  expr: Constraints[40] = <<Parameters>>.foot_hole_seperation
  expr: Constraints[39] = <<Parameters>>.case_spacer_hole
  expr: Constraints[29] = <<Parameters>>.case_width - 1.25in
  expr: Constraints[3] = <<Parameters>>.case_outter_radius * 2
  sketch-geometry (14):
    g0: GeomPoint X=-134.938 Y=15.875 Z=0
    g1: GeomPoint X=134.938 Y=-15.875 Z=0
    g2: ArcOfCircle CenterX=-129.857 CenterY=10.795 CenterZ=0 NormalX=0 NormalY=0 NormalZ=1 AngleXU=0 Radius=5.08 StartAngle=1.5708 EndAngle=3.1416
    g3: ArcOfCircle CenterX=129.858 CenterY=10.795 CenterZ=0 NormalX=0 NormalY=0 NormalZ=1 AngleXU=0 Radius=5.08 StartAngle=6.28318 EndAngle=7.85398
    g4: ArcOfCircle CenterX=129.858 CenterY=-10.795 CenterZ=0 NormalX=0 NormalY=0 NormalZ=1 AngleXU=0 Radius=5.08 StartAngle=4.71239 EndAngle=6.28319
    g5: ArcOfCircle CenterX=-129.857 CenterY=-10.795 CenterZ=0 NormalX=0 NormalY=0 NormalZ=1 AngleXU=0 Radius=5.08 StartAngle=3.14159 EndAngle=4.71239
    g6: LineSegment StartX=-134.937 StartY=10.795 StartZ=0 EndX=-134.937 EndY=-10.795 EndZ=0
    g7: LineSegment StartX=-129.858 StartY=15.875 StartZ=0 EndX=129.858 EndY=15.875 EndZ=0
    g8: LineSegment StartX=134.937 StartY=10.795 StartZ=0 EndX=134.937 EndY=-10.795 EndZ=0
    g9: LineSegment StartX=129.858 StartY=-15.875 StartZ=0 EndX=-129.858 EndY=-15.875 EndZ=0
    g10: Circle CenterX=-100.542 CenterY=6.35 CenterZ=0 NormalX=0 NormalY=0 NormalZ=1 AngleXU=0 Radius=1.55
    g11: Circle CenterX=100.542 CenterY=6.35 CenterZ=0 NormalX=0 NormalY=0 NormalZ=1 AngleXU=0 Radius=1.55
    g12: LineSegment [constr] StartX=-100.542 StartY=6.35 StartZ=0 EndX=0 EndY=6.35 EndZ=0
    g13: LineSegment [constr] StartX=0 StartY=6.35 StartZ=0 EndX=100.542 EndY=6.35 EndZ=0
  constraints (42):
    c: Equal(g5,g2)
    c: Equal(g2,g3)
    c: Equal(g3,g4)
    c: Radius(g2) = 5.08
    c: Horizontal(g7)
    c: Horizontal(g9)
    c: Vertical(g6)
    c: Vertical(g8)
    c: Coincident(g2,g6)
    c: Coincident(g2,g7)
    c: Coincident(g7,g3)
    c: Coincident(g3,g8)
    c: Coincident(g4,g8)
    c: Coincident(g4,g9)
    c: Coincident(g5,g9)
    c: Coincident(g5,g6)
    c: Tangent(g2,g7)
    c: Tangent(g2,g6)
    c: Tangent(g6,g5)
    c: Tangent(g9,g5)
    c: Tangent(g9,g4)
    c: Tangent(g4,g8)
    c: Tangent(g8,g3)
    c: Tangent(g3,g7)
    c: PointOnObject(g0,g7)
    c: PointOnObject(g0,g6)
    c: PointOnObject(g1,g8)
    c: PointOnObject(g1,g9)
    c: Symmetric(g1,g0,g-1)
    c: DistanceX(g0,g1) = 269.875
    c: DistanceY(g1,g0) = 31.75
    c: Coincident(g12,g10)
    c: Coincident(g12,g13)
    c: Coincident(g13,g11)
    c: Horizontal(g12)
    c: Horizontal(g13)
    c: PointOnObject(g12,g-2)
    c: Equal(g13,g12)
    c: Equal(g10,g11)
    c: Diameter(g10) = 3.1
    c: DistanceX(g12,g12) = 100.542
    c: DistanceY(g-1,g12) = 6.35
FEATURE [PartDesign::Pad] Pad007
  Direction = (1,1,1)
  Length = 3.175
  Length2 = 99.9998
  Profile = -> Sketch010
  Type = 0
FEATURE [PartDesign::Body] Body_8
  Group = -> [LCS_0016,Sketch010,Pad007]
  Origin = -> Origin017
  Tip = -> Pad007
COMPONENT P6 — recipe-attached ("foot_2", modeled in this document).
Construction recipe (the document's own serialized feature program — sketch geometry with constraints, then the solid features built on it; lengths are millimeters unless a unit is written):

FEATURE [PartDesign::CoordinateSystem] LCS_0017
  AttacherType = Attacher::AttachEngine3D
  MapMode = 2
  Support = -> [X_Axis018]
FEATURE [Sketcher::SketchObject] Sketch011
  MapMode = 5
  Support = -> [XY_Plane018]
  expr: Constraints[41] = <<Parameters>>.case_screw_hole
  expr: Constraints[40] = <<Parameters>>.foot_hole_seperation
  expr: Constraints[30] = <<Parameters>>.case_width - 1.5in
  expr: Constraints[23] = <<Parameters>>.case_outter_radius * 2
  sketch-geometry (14):
    g0: GeomPoint X=-131.762 Y=12.7 Z=0
    g1: GeomPoint X=131.762 Y=-12.7 Z=0
    g2: ArcOfCircle CenterX=-126.682 CenterY=7.62 CenterZ=0 NormalX=0 NormalY=0 NormalZ=1 AngleXU=0 Radius=5.08 StartAngle=1.57079 EndAngle=3.14159
    g3: ArcOfCircle CenterX=126.682 CenterY=7.62 CenterZ=0 NormalX=0 NormalY=0 NormalZ=1 AngleXU=0 Radius=5.08 StartAngle=2.34623e-07 EndAngle=1.5708
    g4: ArcOfCircle CenterX=126.682 CenterY=-7.62 CenterZ=0 NormalX=0 NormalY=0 NormalZ=1 AngleXU=0 Radius=5.08 StartAngle=4.71239 EndAngle=6.28319
    g5: ArcOfCircle CenterX=-126.682 CenterY=-7.62 CenterZ=0 NormalX=0 NormalY=0 NormalZ=1 AngleXU=0 Radius=5.08 StartAngle=3.14159 EndAngle=4.71239
    g6: LineSegment StartX=-126.682 StartY=12.7 StartZ=0 EndX=126.682 EndY=12.7 EndZ=0
    g7: LineSegment StartX=131.762 StartY=7.62 StartZ=0 EndX=131.762 EndY=-7.62 EndZ=0
    g8: LineSegment StartX=126.682 StartY=-12.7 StartZ=0 EndX=-126.682 EndY=-12.7 EndZ=0
    g9: LineSegment StartX=-131.762 StartY=-7.62 StartZ=0 EndX=-131.762 EndY=7.62 EndZ=0
    g10: Circle CenterX=-100.542 CenterY=6.35 CenterZ=0 NormalX=0 NormalY=0 NormalZ=1 AngleXU=0 Radius=1.05
    g11: Circle CenterX=100.542 CenterY=6.35 CenterZ=0 NormalX=0 NormalY=0 NormalZ=1 AngleXU=0 Radius=1.05
    g12: LineSegment [constr] StartX=-100.542 StartY=6.35 StartZ=0 EndX=0 EndY=6.35 EndZ=0
    g13: LineSegment [constr] StartX=0 StartY=6.35 StartZ=0 EndX=100.542 EndY=6.35 EndZ=0
  constraints (42):
    c: Coincident(g2,g6)
    c: Coincident(g6,g3)
    c: Coincident(g3,g7)
    c: Coincident(g7,g4)
    c: Coincident(g4,g8)
    c: Coincident(g8,g5)
    c: Coincident(g5,g9)
    c: Coincident(g9,g2)
    c: Tangent(g2,g6)
    c: Tangent(g6,g3)
    c: Tangent(g3,g7)
    c: Tangent(g7,g4)
    c: Tangent(g4,g8)
    c: Tangent(g8,g5)
    c: Tangent(g5,g9)
    c: Tangent(g9,g2)
    c: Vertical(g9)
    c: Vertical(g7)
    c: Horizontal(g6)
    c: Horizontal(g8)
    c: Equal(g4,g3)
    c: Equal(g3,g2)
    c: Equal(g2,g5)
    c: Radius(g3) = 5.08
    c: PointOnObject(g0,g6)
    c: PointOnObject(g0,g9)
    c: PointOnObject(g1,g7)
    c: PointOnObject(g1,g8)
    c: Symmetric(g0,g1,g-1)
    c: DistanceY(g1,g0) = 25.4
    c: DistanceX(g0,g1) = 263.525
    c: Coincident(g12,g13)
    c: Coincident(g12,g10)
    c: Coincident(g13,g11)
    c: Horizontal(g12)
    c: Horizontal(g13)
    c: PointOnObject(g12,g-2)
    c: DistanceY(g-1,g12) = 6.35
    c: Equal(g10,g11)
    c: Equal(g13,g12)
    c: DistanceX(g12,g12) = 100.542
    c: Diameter(g10) = 2.1
FEATURE [PartDesign::Pad] Pad008
  Direction = (1,1,1)
  Length = 3.175
  Length2 = 99.9998
  Profile = -> Sketch011
  Type = 0
FEATURE [PartDesign::Body] Body_9
  Group = -> [LCS_0017,Sketch011,Pad008]
  Origin = -> Origin018
  Tip = -> Pad008
COMPONENT P7 — geometry summary ("switch_plate"; its construction recipe is too large to include in this document):
  bounding box: 301.6 x 136.5 x 1.6 mm
  tessellated surface: 2,048 triangles
  volume: 1616300518331806587004992306477167730326482490091380081681507924902768365290733470482432 mm^3 (2472457778803261945290329439255520156992795221368578984776961897746904182315624169472% of its bounding box)
  symmetry: mirror-symmetric across its z mid-plane
COMPONENT P8 — recipe-attached ("usb_spacer", modeled in this document).
Construction recipe (the document's own serialized feature program — sketch geometry with constraints, then the solid features built on it; lengths are millimeters unless a unit is written):

FEATURE [PartDesign::CoordinateSystem] LCS_0005
  AttacherType = Attacher::AttachEngine3D
  MapMode = 2
  Support = -> [X_Axis006]
FEATURE [Sketcher::SketchObject] Sketch002
  MapMode = 5
  Support = -> [XY_Plane006]
  expr: Constraints[24] = <<Parameters>>.case_width
  expr: Constraints[25] = <<Parameters>>.case_height
  expr: Constraints[51] = <<Parameters>>.case_edge_width - <<Parameters>>.case_edge_relief
  expr: Constraints[122] = <<Parameters>>.case_hole_edge_dist
  expr: Constraints[19] = <<Parameters>>.case_outter_radius
  expr: Constraints[50] = <<Parameters>>.case_inner_radius
  expr: Constraints[52] = <<Parameters>>.case_edge_width - <<Parameters>>.case_edge_relief
  expr: Constraints[53] = <<Parameters>>.case_edge_width - <<Parameters>>.case_edge_relief
  expr: Constraints[54] = <<Parameters>>.case_edge_width - <<Parameters>>.case_edge_relief
  expr: Constraints[58] = <<Parameters>>.case_inner_radius
  expr: Constraints[87] = <<Parameters>>.usb_cutout_width
  expr: Constraints[121] = <<Parameters>>.case_hole_edge_dist
  expr: Constraints[86] = <<Parameters>>.usb_offset
  expr: Constraints[95] = <<Parameters>>.case_spacer_hole
  expr: Constraints[120] = <<Parameters>>.case_hole_edge_dist
  sketch-geometry (41):
    g0: LineSegment [constr] StartX=-148.273 StartY=68.2625 StartZ=0 EndX=148.273 EndY=68.2625 EndZ=0
    g1: LineSegment StartX=-150.812 StartY=65.7225 StartZ=0 EndX=-150.812 EndY=-65.7225 EndZ=0
    g2: LineSegment StartX=-148.272 StartY=-68.2625 StartZ=0 EndX=148.273 EndY=-68.2625 EndZ=0
    g3: LineSegment StartX=150.813 StartY=65.7225 StartZ=0 EndX=150.813 EndY=-65.7225 EndZ=0
    g4: ArcOfCircle CenterX=-148.272 CenterY=65.7225 CenterZ=0 NormalX=0 NormalY=0 NormalZ=1 AngleXU=0 Radius=2.54 StartAngle=1.5708 EndAngle=3.14159
    g5: ArcOfCircle CenterX=148.273 CenterY=65.7225 CenterZ=0 NormalX=0 NormalY=0 NormalZ=1 AngleXU=0 Radius=2.54 StartAngle=5.25631e-06 EndAngle=1.5708
    g6: ArcOfCircle CenterX=148.273 CenterY=-65.7225 CenterZ=0 NormalX=0 NormalY=0 NormalZ=1 AngleXU=0 Radius=2.54 StartAngle=4.71239 EndAngle=6.28319
    g7: ArcOfCircle CenterX=-148.272 CenterY=-65.7225 CenterZ=0 NormalX=0 NormalY=0 NormalZ=1 AngleXU=0 Radius=2.54 StartAngle=3.14159 EndAngle=4.71239
    g8: ArcOfCircle CenterX=-142.399 CenterY=59.8488 CenterZ=0 NormalX=0 NormalY=0 NormalZ=1 AngleXU=0 Radius=1.27 StartAngle=1.5708 EndAngle=3.1416
    g9: ArcOfCircle CenterX=-142.399 CenterY=-59.8487 CenterZ=0 NormalX=0 NormalY=0 NormalZ=1 AngleXU=0 Radius=1.27 StartAngle=3.14159 EndAngle=4.71239
    g10: ArcOfCircle CenterX=142.399 CenterY=-59.8487 CenterZ=0 NormalX=0 NormalY=0 NormalZ=1 AngleXU=0 Radius=1.27 StartAngle=4.71239 EndAngle=6.28319
    g11: ArcOfCircle CenterX=142.399 CenterY=59.8488 CenterZ=0 NormalX=0 NormalY=0 NormalZ=1 AngleXU=0 Radius=1.27 StartAngle=6.28318 EndAngle=7.85398
    g12: LineSegment [constr] StartX=-142.399 StartY=61.1187 StartZ=0 EndX=142.399 EndY=61.1187 EndZ=0
    g13: LineSegment StartX=-143.669 StartY=59.8487 StartZ=0 EndX=-143.669 EndY=-59.8488 EndZ=0
    g14: LineSegment StartX=-142.399 StartY=-61.1187 StartZ=0 EndX=142.399 EndY=-61.1187 EndZ=0
    g15: LineSegment StartX=143.669 StartY=-59.8487 StartZ=0 EndX=143.669 EndY=59.8487 EndZ=0
    g16: LineSegment StartX=-142.399 StartY=61.1187 StartZ=0 EndX=93.345 EndY=61.1187 EndZ=0
    g17: LineSegment StartX=94.615 StartY=62.3887 StartZ=0 EndX=94.615 EndY=66.9925 EndZ=0
    g18: LineSegment StartX=93.345 StartY=68.2625 StartZ=0 EndX=-148.273 EndY=68.2625 EndZ=0
    g19: LineSegment StartX=108.585 StartY=68.2625 StartZ=0 EndX=148.273 EndY=68.2625 EndZ=0
    g20: LineSegment StartX=142.399 StartY=61.1187 StartZ=0 EndX=108.585 EndY=61.1188 EndZ=0
    g21: LineSegment StartX=107.315 StartY=62.3888 StartZ=0 EndX=107.315 EndY=66.9925 EndZ=0
    g22: ArcOfCircle CenterX=108.585 CenterY=66.9925 CenterZ=0 NormalX=0 NormalY=0 NormalZ=1 AngleXU=0 Radius=1.27 StartAngle=1.5708 EndAngle=3.14159
    g23: ArcOfCircle CenterX=108.585 CenterY=62.3888 CenterZ=0 NormalX=0 NormalY=0 NormalZ=1 AngleXU=0 Radius=1.27 StartAngle=3.14159 EndAngle=4.71238
    g24: ArcOfCircle CenterX=93.345 CenterY=66.9925 CenterZ=0 NormalX=0 NormalY=0 NormalZ=1 AngleXU=0 Radius=1.27 StartAngle=7.44682e-07 EndAngle=1.5708
    g25: ArcOfCircle CenterX=93.345 CenterY=62.3887 CenterZ=0 NormalX=0 NormalY=0 NormalZ=1 AngleXU=0 Radius=1.27 StartAngle=4.71239 EndAngle=6.28318
    g26: GeomPoint X=100.965 Y=64.6906 Z=0
    g27: Circle CenterX=-146.844 CenterY=64.2937 CenterZ=0 NormalX=0 NormalY=0 NormalZ=1 AngleXU=0 Radius=1.55
    g28: Circle CenterX=-48.9479 CenterY=64.2937 CenterZ=0 NormalX=0 NormalY=0 NormalZ=1 AngleXU=0 Radius=1.55
    g29: Circle CenterX=48.9479 CenterY=64.2937 CenterZ=0 NormalX=0 NormalY=0 NormalZ=1 AngleXU=0 Radius=1.55
    g30: Circle CenterX=146.844 CenterY=64.2937 CenterZ=0 NormalX=0 NormalY=0 NormalZ=1 AngleXU=0 Radius=1.55
    g31: Circle CenterX=-146.844 CenterY=-64.2937 CenterZ=0 NormalX=0 NormalY=0 NormalZ=1 AngleXU=0 Radius=1.55
    g32: Circle CenterX=-48.9479 CenterY=-64.2937 CenterZ=0 NormalX=0 NormalY=0 NormalZ=1 AngleXU=0 Radius=1.55
    g33: Circle CenterX=48.9479 CenterY=-64.2937 CenterZ=0 NormalX=0 NormalY=0 NormalZ=1 AngleXU=0 Radius=1.55
    g34: Circle CenterX=146.844 CenterY=-64.2937 CenterZ=0 NormalX=0 NormalY=0 NormalZ=1 AngleXU=0 Radius=1.55
    g35: LineSegment [constr] StartX=-146.844 StartY=64.2937 StartZ=0 EndX=-48.9479 EndY=64.2937 EndZ=0
    g36: LineSegment [constr] StartX=-48.9479 StartY=64.2937 StartZ=0 EndX=48.9479 EndY=64.2937 EndZ=0
    g37: LineSegment [constr] StartX=48.9479 StartY=64.2937 StartZ=0 EndX=146.844 EndY=64.2937 EndZ=0
    g38: LineSegment [constr] StartX=-146.844 StartY=-64.2937 StartZ=0 EndX=-48.9479 EndY=-64.2937 EndZ=0
    g39: LineSegment [constr] StartX=-48.9479 StartY=-64.2937 StartZ=0 EndX=48.9479 EndY=-64.2937 EndZ=0
    g40: LineSegment [constr] StartX=48.9479 StartY=-64.2937 StartZ=0 EndX=146.844 EndY=-64.2937 EndZ=0
  constraints (123):
    c: Coincident(g4,g0)
    c: Coincident(g4,g1)
    c: Coincident(g1,g7)
    c: Coincident(g7,g2)
    c: Coincident(g6,g2)
    c: Coincident(g3,g6)
    c: Coincident(g0,g5)
    c: Coincident(g3,g5)
    c: Tangent(g4,g0)
    c: Tangent(g4,g1)
    c: Tangent(g1,g7)
    c: Tangent(g7,g2)
    c: Tangent(g2,g6)
    c: Tangent(g6,g3)
    c: Tangent(g3,g5)
    c: Tangent(g5,g0)
    c: Equal(g4,g5)
    c: Equal(g5,g6)
    c: Equal(g6,g7)
    c: Radius(g4) = 2.54
    c: Vertical(g1)
    c: Vertical(g3)
    c: Horizontal(g0)
    c: Horizontal(g2)
    c: DistanceX(g1,g3) = 301.625
    c: DistanceY(g2,g5) = 136.525
    c: Symmetric(g4,g2,g-1)
    c: Horizontal(g12)
    c: Horizontal(g14)
    c: Vertical(g13)
    c: Vertical(g15)
    c: Coincident(g12,g8)
    c: Coincident(g13,g8)
    c: Coincident(g9,g13)
    c: Coincident(g9,g14)
    c: Coincident(g14,g10)
    c: Coincident(g10,g15)
    c: Coincident(g15,g11)
    c: Coincident(g12,g11)
    c: Equal(g8,g9)
    c: Equal(g9,g10)
    c: Equal(g10,g11)
    c: Tangent(g12,g8)
    c: Tangent(g8,g13)
    c: Tangent(g13,g9)
    c: Tangent(g9,g14)
    c: Tangent(g14,g10)
    c: Tangent(g10,g15)
    c: Tangent(g15,g11)
    c: Tangent(g11,g12)
    c: Radius(g8) = 1.27
    c: DistanceX(g1,g8) = 7.14375
    c: DistanceY(g8,g4) = 7.14375
    c: DistanceY(g2,g10) = 7.14375
    c: DistanceX(g10,g3) = 7.14375
    c: Equal(g25,g23)
    c: Equal(g23,g22)
    c: Equal(g22,g24)
    c: Radius(g24) = 1.27
    c: Coincident(g18,g24)
    c: Coincident(g24,g17)
    c: Coincident(g25,g17)
    c: Coincident(g16,g25)
    c: Coincident(g23,g21)
    c: Coincident(g21,g22)
    c: Coincident(g22,g19)
    c: Coincident(g23,g20)
    c: Coincident(g20,g11)
    c: Coincident(g19,g5)
    c: Coincident(g18,g4)
    c: Coincident(g16,g8)
    c: Tangent(g18,g24)
    c: Tangent(g17,g24)
    c: Tangent(g17,g25)
    c: Tangent(g25,g16)
    c: Tangent(g23,g21)
    c: Tangent(g23,g20)
    c: Tangent(g21,g22)
    c: Tangent(g22,g19)
    c: PointOnObject(g19,g0)
    c: PointOnObject(g20,g12)
    c: PointOnObject(g18,g0)
    c: PointOnObject(g16,g12)
    c: Vertical(g17)
    c: Vertical(g21)
    c: Symmetric(g17,g21,g26)
    c: DistanceX(g26,g3) = 49.8475
    c: DistanceX(g17,g21) = 12.7
    c: Equal(g27,g28)
    c: Equal(g28,g29)
    c: Equal(g29,g30)
    c: Equal(g30,g34)
    c: Equal(g34,g33)
    c: Equal(g33,g32)
    c: Equal(g32,g31)
    c: Diameter(g27) = 3.1
    c: Coincident(g35,g27)
    c: Coincident(g36,g35)
    c: Coincident(g35,g28)
    c: Coincident(g36,g37)
    c: Coincident(g36,g29)
    c: Coincident(g37,g30)
    c: Coincident(g38,g31)
    c: Coincident(g38,g32)
    c: Coincident(g39,g32)
    c: Coincident(g39,g33)
    c: Coincident(g40,g33)
    c: Coincident(g34,g40)
    c: Equal(g40,g39)
    c: Equal(g39,g38)
    c: Equal(g38,g35)
    c: Equal(g35,g36)
    c: Equal(g36,g37)
    c: Horizontal(g35)
    c: Horizontal(g36)
    c: Horizontal(g37)
    c: Horizontal(g40)
    c: Horizontal(g39)
    c: Horizontal(g38)
    c: Symmetric(g28,g33,g-1)
    c: DistanceX(g34,g3) = 3.96875
    c: DistanceY(g2,g34) = 3.96875
    c: DistanceX(g1,g31) = 3.96875
FEATURE [PartDesign::Pad] Pad002
  Direction = (1,1,1)
  Length = 3.175
  Length2 = 99.9998
  Profile = -> Sketch002
  Type = 0
FEATURE [PartDesign::Body] Body_3
  Group = -> [LCS_0005,Sketch002,Pad002]
  Origin = -> Origin006
  Tip = -> Pad002
PROVENANCE & LICENSES
A FreeCAD (.FCStd) document from a public repository crawl; recipes are the document's own serialized feature recipes (and, for linked parts, companion documents' recipes).
License: mit.
